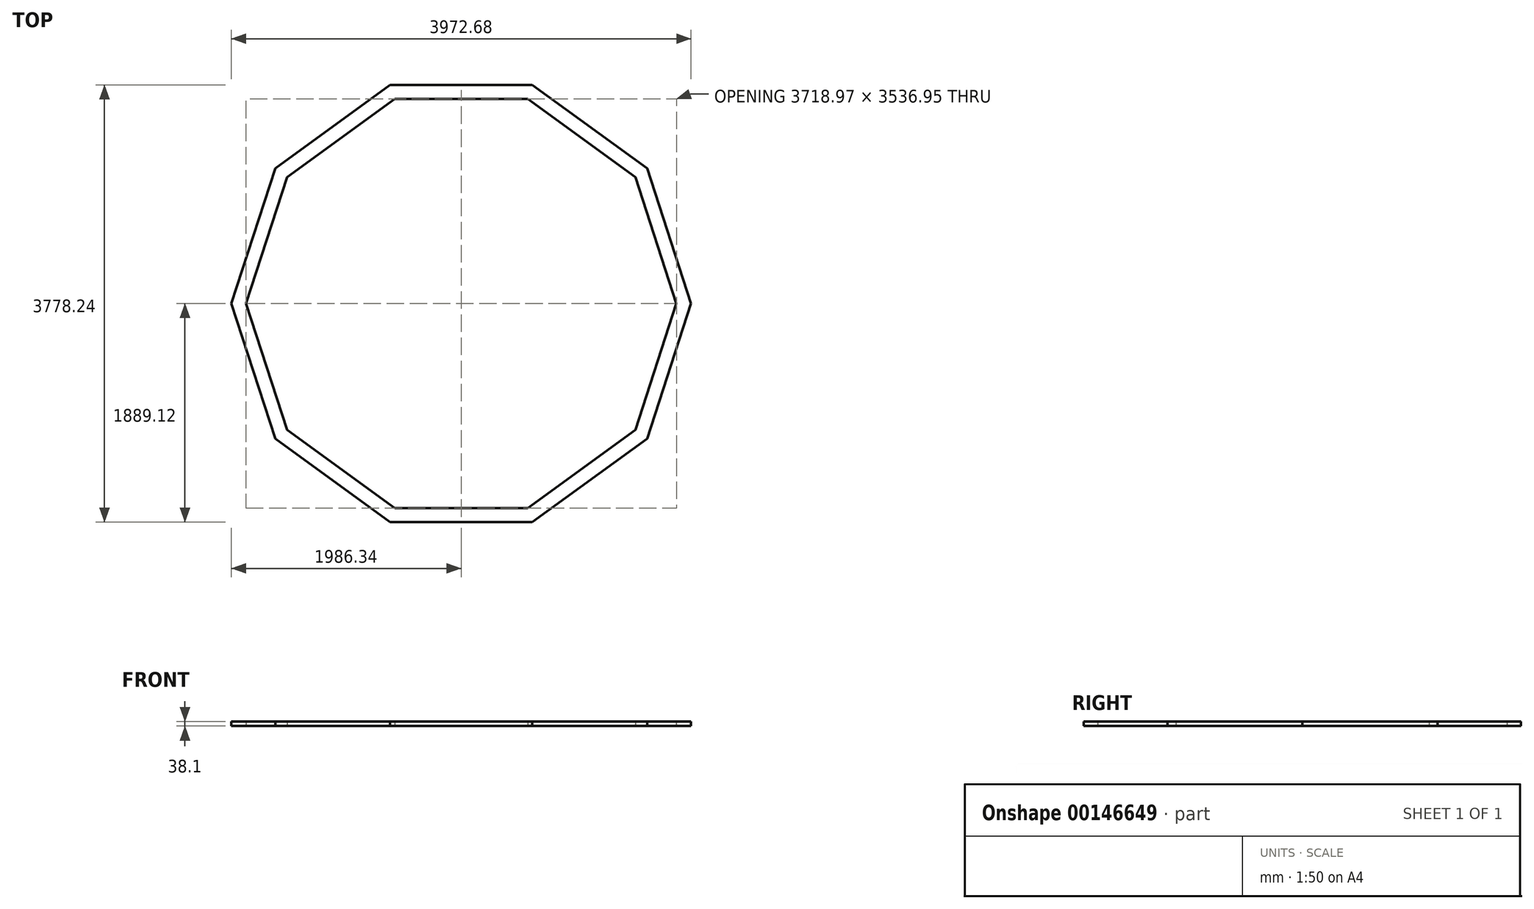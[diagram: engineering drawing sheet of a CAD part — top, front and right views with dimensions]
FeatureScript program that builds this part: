
annotation { "Feature Type Name" : "Feature", "Feature Type Description" : "" }
export const myFeature = defineFeature(function(context is Context, id is Id, definition is map)
    precondition{}
    {
        {
            var Q0;
            Q0=qCreatedBy(makeId("Top.planeOp"),FACE);
            var sketch = newSketch(context, id + "F0", { "sketchPlane" : qUnion([Q0])});
            skCircle(sketch, "E0.cCircle", {"center": v(0, 0) * mm, "radius": 1768.48 * mm, "construction": true});
            skLineSegment(sketch, "E0.0", {"start": v(-574.61, 1768.48) * mm, "end": v(574.61, 1768.48) * mm});
            skLineSegment(sketch, "E0.1", {"start": v(574.61, 1768.47) * mm, "end": v(1504.35, 1092.98) * mm});
            skLineSegment(sketch, "E0.2", {"start": v(1504.35, 1092.98) * mm, "end": v(1859.48, 0) * mm});
            skLineSegment(sketch, "E0.3", {"start": v(1859.48, 0) * mm, "end": v(1504.35, -1092.98) * mm});
            skLineSegment(sketch, "E0.4", {"start": v(1504.35, -1092.98) * mm, "end": v(574.61, -1768.48) * mm});
            skLineSegment(sketch, "E0.5", {"start": v(574.61, -1768.48) * mm, "end": v(-574.61, -1768.48) * mm});
            skLineSegment(sketch, "E0.6", {"start": v(-574.61, -1768.48) * mm, "end": v(-1504.35, -1092.98) * mm});
            skLineSegment(sketch, "E0.7", {"start": v(-1504.35, -1092.98) * mm, "end": v(-1859.48, 0) * mm});
            skLineSegment(sketch, "E0.8", {"start": v(-1859.48, 0) * mm, "end": v(-1504.35, 1092.98) * mm});
            skLineSegment(sketch, "E0.9", {"start": v(-1504.35, 1092.98) * mm, "end": v(-574.61, 1768.48) * mm});
            skPoint(sketch, "E0.0.midPoint", {"position": v(0, 1768.48) * mm});
            skCircle(sketch, "E1.cCircle", {"center": v(0, 0) * mm, "radius": 1889.13 * mm, "construction": true});
            skLineSegment(sketch, "E1.0", {"start": v(-613.81, 1889.13) * mm, "end": v(613.81, 1889.13) * mm});
            skLineSegment(sketch, "E1.1", {"start": v(613.81, 1889.12) * mm, "end": v(1606.99, 1167.54) * mm});
            skLineSegment(sketch, "E1.2", {"start": v(1606.99, 1167.54) * mm, "end": v(1986.34, 0) * mm});
            skLineSegment(sketch, "E1.3", {"start": v(1986.34, 0) * mm, "end": v(1606.99, -1167.54) * mm});
            skLineSegment(sketch, "E1.4", {"start": v(1606.99, -1167.54) * mm, "end": v(613.81, -1889.13) * mm});
            skLineSegment(sketch, "E1.5", {"start": v(613.81, -1889.12) * mm, "end": v(-613.81, -1889.13) * mm});
            skLineSegment(sketch, "E1.6", {"start": v(-613.81, -1889.13) * mm, "end": v(-1606.99, -1167.54) * mm});
            skLineSegment(sketch, "E1.7", {"start": v(-1606.99, -1167.54) * mm, "end": v(-1986.34, 0) * mm});
            skLineSegment(sketch, "E1.8", {"start": v(-1986.34, 0) * mm, "end": v(-1606.99, 1167.54) * mm});
            skLineSegment(sketch, "E1.9", {"start": v(-1606.99, 1167.54) * mm, "end": v(-613.81, 1889.12) * mm});
            skPoint(sketch, "E1.0.midPoint", {"position": v(0, 1889.13) * mm});
            skSolve(sketch);
        }
        {
            var Q0;
            Q0 = qSketchRegion(id + "F0", true);
            extrude(context, id + "F1", {"entities" : qUnion([Q0]), "depth" : 38.1 * mm});
        }
    });
